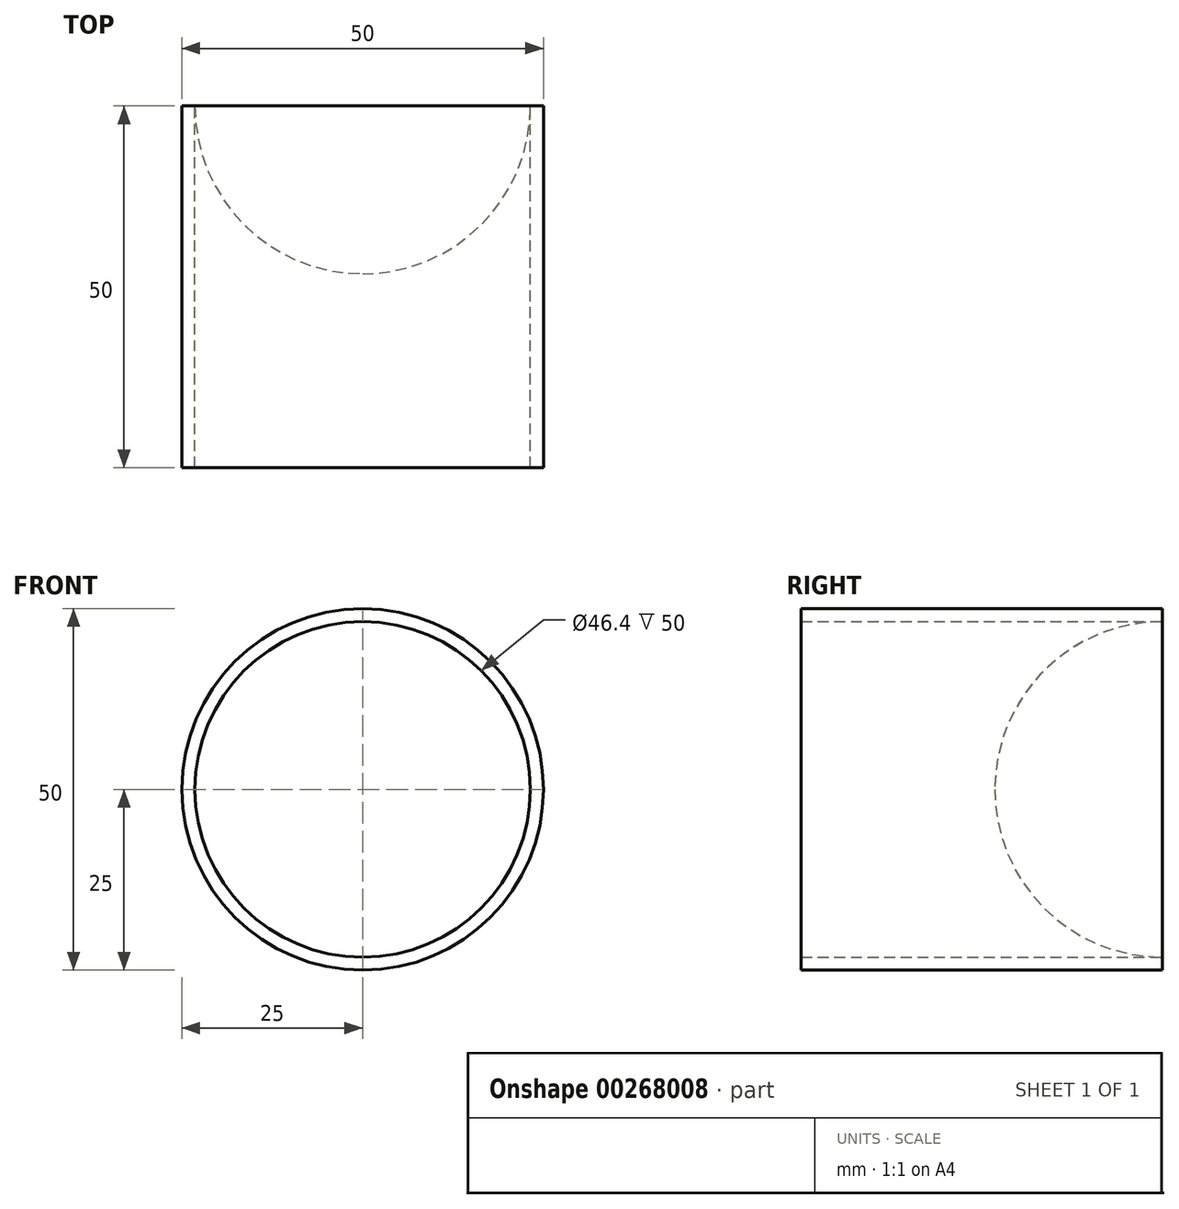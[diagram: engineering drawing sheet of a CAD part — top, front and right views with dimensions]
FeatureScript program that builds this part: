
annotation { "Feature Type Name" : "Feature", "Feature Type Description" : "" }
export const myFeature = defineFeature(function(context is Context, id is Id, definition is map)
    precondition{}
    {
        {
            assignVariable(context, id + "F0", {"name" : "OuterDiameter", "anyValue" : 50});
        }
        {
            var Q0;
            Q0=qCreatedBy(makeId("Front.planeOp"),FACE);
            var sketch = newSketch(context, id + "F1", { "sketchPlane" : qUnion([Q0])});
            skCircle(sketch, "E0", {"center": v(0, 0) * mm, "radius": 25 * mm});
            skCircle(sketch, "E1.0", {"center": v(0, 0) * mm, "radius": 23.2 * mm});
            skSolve(sketch);
        }
        {
            var Q0;
            Q0 = qSketchRegion(id + "F1", true);
            extrude(context, id + "F2", {"entities" : qUnion([Q0]), "depth" : (getVariable(context, 'OuterDiameter')) * mm});
        }
        {
            var Q0;
            Q0=qCreatedBy(makeId("Right.planeOp"),FACE);
            var sketch = newSketch(context, id + "F3", { "sketchPlane" : qUnion([Q0])});
            skArc(sketch, "E2", {"start": v(0, 23.2) * mm, "mid": v(-16.4, 16.4) * mm, "end": v(-23.2, 0) * mm});
            skLineSegment(sketch, "E3", {"start": v(-23.2, 0) * mm, "end": v(0, 0) * mm});
            skLineSegment(sketch, "E4", {"start": v(0, 0) * mm, "end": v(0, 23.2) * mm});
            skSolve(sketch);
        }
        {
            var Q0;
            Q0=makeQuery(id+"F3.imprint","IMPRINT",FACE,{"disambiguationData":[TD([[makeQuery(id+"F3.imprint","IMPRINT",EDGE,{"derivedFrom":sQuery(id+"F3.wireOp",EDGE,"E2")}),1.0]])]});
            var Q1;
            Q1=sQuery(id+"F3.wireOp",EDGE,"E3");
            revolve(context, id + "F4", {"entities" : qUnion([Q0]), "axis" : qUnion([Q1]), "revolveType" : RevolveType.FULL});
        }
    });
